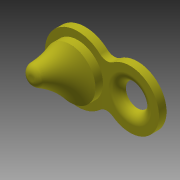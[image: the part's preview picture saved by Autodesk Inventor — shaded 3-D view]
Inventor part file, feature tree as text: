
AUTODESK INVENTOR PART (.ipt)
format: ipt  version: 2015 (Build 190159000, 159)  size: 245,760 bytes
history: native  units: mm
features: extrude x6, sketch x6, fillet x5, other x1
ambient origin geometry x8: Origin, YZ Plane, XZ Plane, XY Plane, X Axis, Y Axis, Z Axis, Center Point
bodies: Body1 (feature_tree)
feature tree (18):
  other  "Sólido1"
  extrude  "Extrusión1"  Depth=3.0mm TaperAngle=0.0deg
  extrude  "Extrusión2"  Depth=3.0mm TaperAngle=0.0deg
  fillet  "Empalme1"  Radius=3.0mm
  fillet  "Empalme2"  Radius=20.0mm
  fillet  "Empalme3"  Radius=20.0mm
  extrude  "Extrusión3"  Depth=23.0mm
  extrude  "Extrusión4"  Depth=3.0mm TaperAngle=0.0deg
  extrude  "Extrusión5"  Depth=3.0mm TaperAngle=0.0deg
  fillet  "Empalme4"  Radius=1.0mm
  extrude  "Extrusión6"  Depth=4.0mm TaperAngle=0.0deg
  fillet  "Empalme5"  Radius=4.0mm
  sketch  "Boceto1"  dims[d0=20.0mm d1=3.0mm d2=0.0mm]
  sketch  "Boceto2"  dims[d3=8.0mm d4=9.5mm d5=0.0mm d6=3.0mm d7=20.0mm d8=20.0mm]
  sketch  "Boceto3"  dims[d11=17.0mm d12=23.0mm]
  sketch  "Boceto4"  dims[d13=26.0mm d14=3.0mm d15=0.0mm]
  sketch  "Boceto5"  dims[d16=4.0mm d17=3.0mm d18=0.0mm d19=1.0mm d20=0.0mm]
  sketch  "Boceto6"  dims[d21=4.0mm d22=1.0mm d23=0.0mm d24=4.0mm]
